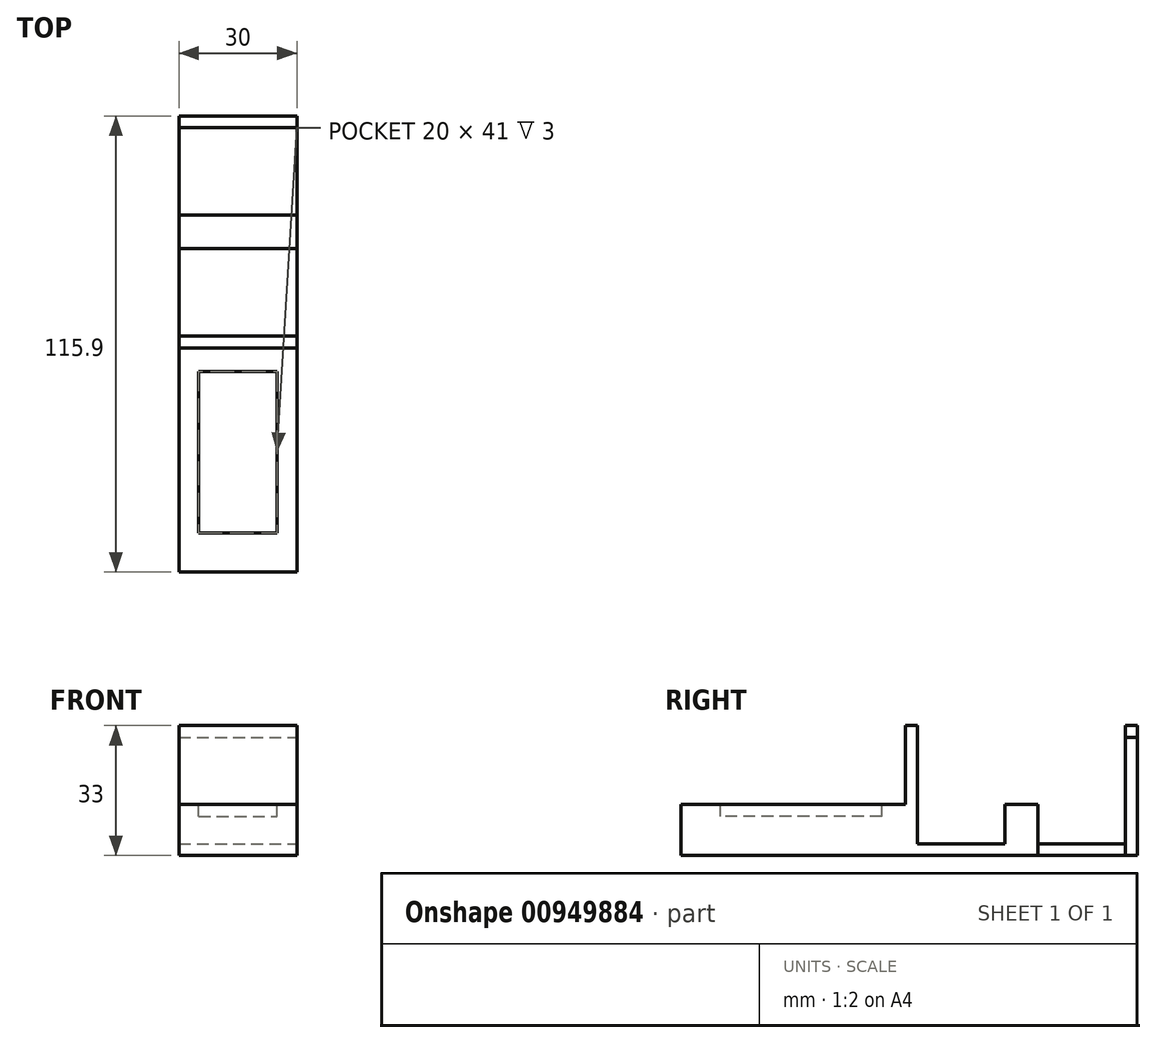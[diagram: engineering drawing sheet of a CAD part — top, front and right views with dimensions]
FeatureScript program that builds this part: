
annotation { "Feature Type Name" : "Feature", "Feature Type Description" : "" }
export const myFeature = defineFeature(function(context is Context, id is Id, definition is map)
    precondition{}
    {
        {
            var Q0;
            Q0=qCreatedBy(makeId("Top.planeOp"),FACE);
            var sketch = newSketch(context, id + "F0", { "sketchPlane" : qUnion([Q0])});
            skLineSegment(sketch, "E0.bottom", {"start": v(82.85, 0) * mm, "end": v(52.85, 0) * mm});
            skLineSegment(sketch, "E0.top", {"start": v(82.85, 115.9) * mm, "end": v(52.85, 115.9) * mm});
            skPoint(sketch, "E0.middle", {"position": v(67.85, 57.95) * mm});
            skLineSegment(sketch, "E1.bottom", {"start": v(52.85, 57) * mm, "end": v(82.85, 57) * mm});
            skLineSegment(sketch, "E1.top", {"start": v(52.85, 60) * mm, "end": v(82.85, 60) * mm});
            skLineSegment(sketch, "E1.left", {"start": v(52.85, 57) * mm, "end": v(52.85, 60) * mm});
            skLineSegment(sketch, "E1.right", {"start": v(82.85, 57) * mm, "end": v(82.85, 60) * mm});
            skLineSegment(sketch, "E2.bottom", {"start": v(52.85, 82.2) * mm, "end": v(82.85, 82.2) * mm});
            skLineSegment(sketch, "E2.top", {"start": v(52.85, 90.7) * mm, "end": v(82.85, 90.7) * mm});
            skLineSegment(sketch, "E2.left", {"start": v(52.85, 82.2) * mm, "end": v(52.85, 90.7) * mm});
            skLineSegment(sketch, "E2.right", {"start": v(82.85, 82.2) * mm, "end": v(82.85, 90.7) * mm});
            skLineSegment(sketch, "E3.bottom", {"start": v(52.85, 112.9) * mm, "end": v(82.85, 112.9) * mm});
            skLineSegment(sketch, "E3.top", {"start": v(52.85, 115.9) * mm, "end": v(82.85, 115.9) * mm});
            skLineSegment(sketch, "E3.left", {"start": v(52.85, 112.9) * mm, "end": v(52.85, 115.9) * mm});
            skLineSegment(sketch, "E3.right", {"start": v(82.85, 112.9) * mm, "end": v(82.85, 115.9) * mm});
            skLineSegment(sketch, "E4", {"start": v(52.85, 0) * mm, "end": v(52.85, 57) * mm});
            skLineSegment(sketch, "E5", {"start": v(52.85, 60) * mm, "end": v(52.85, 82.2) * mm});
            skLineSegment(sketch, "E6", {"start": v(52.85, 90.7) * mm, "end": v(52.85, 112.9) * mm});
            skLineSegment(sketch, "E7", {"start": v(82.85, 112.9) * mm, "end": v(82.85, 90.7) * mm});
            skLineSegment(sketch, "E8", {"start": v(82.85, 82.2) * mm, "end": v(82.85, 60) * mm});
            skLineSegment(sketch, "E9", {"start": v(82.85, 57) * mm, "end": v(82.85, 0) * mm});
            skSolve(sketch);
        }
        {
            var Q0;
            Q0 = qSketchRegion(id + "F0", true);
            extrude(context, id + "F1", {"entities" : qUnion([Q0]), "depth" : 3 * mm, "offsetDistance" : 25 * mm});
        }
        {
            var Q0;
            Q0=makeQuery(id+"F0.imprint","IMPRINT",FACE,{"disambiguationData":[TD([[makeQuery(id+"F0.imprint","IMPRINT",EDGE,{"derivedFrom":sQuery(id+"F0.wireOp",EDGE,"E1.bottom")}),1.0]])]});
            var Q1;
            Q1=makeQuery(id+"F0.imprint","IMPRINT",FACE,{"disambiguationData":[TD([[makeQuery(id+"F0.imprint","IMPRINT",EDGE,{"derivedFrom":sQuery(id+"F0.wireOp",EDGE,"E3.bottom")}),1.0]])]});
            extrude(context, id + "F2", {"entities" : qUnion([Q0, Q1]), "operationType" : NewBodyOperationType.ADD, "depth" : 30 * mm, "offsetDistance" : 25 * mm});
        }
        {
            var Q0;
            Q0=makeQuery(id+"F0.imprint","IMPRINT",FACE,{"disambiguationData":[TD([[makeQuery(id+"F0.imprint","IMPRINT",EDGE,{"derivedFrom":sQuery(id+"F0.wireOp",EDGE,"E2.bottom")}),1.0]])]});
            extrude(context, id + "F3", {"entities" : qUnion([Q0]), "operationType" : NewBodyOperationType.ADD, "depth" : 13 * mm, "offsetDistance" : 25 * mm});
        }
        {
            var Q0;
            {var subQ0=sQuery(id+"F0.wireOp",EDGE,"E9");var subQ1=sQuery(id+"F0.wireOp",EDGE,"E8");var subQ2=sQuery(id+"F0.wireOp",EDGE,"E7");var subQ3=sQuery(id+"F0.wireOp",EDGE,"E3.right");var subQ4=sQuery(id+"F0.wireOp",EDGE,"E2.right");var subQ5=sQuery(id+"F0.wireOp",EDGE,"E1.right");var subQ6=sQuery(id+"F0.wireOp",EDGE,"E6");var subQ7=sQuery(id+"F0.wireOp",EDGE,"E5");var subQ8=sQuery(id+"F0.wireOp",EDGE,"E4");var subQ9=sQuery(id+"F0.wireOp",EDGE,"E3.left");var subQ10=sQuery(id+"F0.wireOp",EDGE,"E2.left");var subQ11=sQuery(id+"F0.wireOp",EDGE,"E1.left");var subQ12=sQuery(id+"F0.wireOp",EDGE,"E0.bottom");Q0=makeQuery(id+"F2.boolean.opBoolean","SPLIT",FACE,{"disambiguationData":[TD([makeQuery(id+"F1.opExtrude","SWEPT_FACE",FACE,{"disambiguationData":[OSD([subQ12])]})])],"derivedFrom":makeQuery(id+"F1.opExtrude","CAP_FACE",FACE,{"disambiguationData":[OSD([subQ12,subQ11,subQ5,subQ10,subQ4,sQuery(id+"F0.wireOp",EDGE,"E3.top"),subQ9,subQ3,subQ8,subQ7,subQ6,subQ2,subQ1,subQ0])],"isStart":false})});}
            extrude(context, id + "F4", {"entities" : qUnion([Q0]), "operationType" : NewBodyOperationType.ADD, "depth" : 10 * mm, "offsetDistance" : 25 * mm});
        }
        {
            var Q0;
            Q0=makeQuery(id+"F4.opExtrude","CAP_FACE",FACE,{"disambiguationData":[OSD([sQuery(id+"F0.wireOp",EDGE,"E0.bottom"),sQuery(id+"F0.wireOp",EDGE,"E1.left"),sQuery(id+"F0.wireOp",EDGE,"E1.right"),sQuery(id+"F0.wireOp",EDGE,"E2.left"),sQuery(id+"F0.wireOp",EDGE,"E2.right"),sQuery(id+"F0.wireOp",EDGE,"E3.top"),sQuery(id+"F0.wireOp",EDGE,"E3.left"),sQuery(id+"F0.wireOp",EDGE,"E3.right"),sQuery(id+"F0.wireOp",EDGE,"E4"),sQuery(id+"F0.wireOp",EDGE,"E5"),sQuery(id+"F0.wireOp",EDGE,"E6"),sQuery(id+"F0.wireOp",EDGE,"E7"),sQuery(id+"F0.wireOp",EDGE,"E8"),sQuery(id+"F0.wireOp",EDGE,"E9")])],"isStart":false});
            var sketch = newSketch(context, id + "F5", { "sketchPlane" : qUnion([Q0])});
            skLineSegment(sketch, "E10.bottom", {"start": v(77.85, 10) * mm, "end": v(57.85, 10) * mm});
            skLineSegment(sketch, "E10.top", {"start": v(77.85, 51) * mm, "end": v(57.85, 51) * mm});
            skLineSegment(sketch, "E10.left", {"start": v(77.85, 10) * mm, "end": v(77.85, 51) * mm});
            skLineSegment(sketch, "E10.right", {"start": v(57.85, 10) * mm, "end": v(57.85, 51) * mm});
            skPoint(sketch, "E10.middle", {"position": v(67.85, 30.5) * mm});
            skSolve(sketch);
        }
        {
            var Q0;
            Q0=makeQuery(id+"F5.imprint","IMPRINT",FACE,{"disambiguationData":[TD([[makeQuery(id+"F5.imprint","IMPRINT",EDGE,{"derivedFrom":sQuery(id+"F5.wireOp",EDGE,"E10.bottom")}),-1.0]])]});
            extrude(context, id + "F6", {"entities" : qUnion([Q0]), "operationType" : NewBodyOperationType.REMOVE, "endBound" : BoundingType.UP_TO_NEXT, "oppositeDirection" : true, "depth" : 25 * mm, "offsetDistance" : 25 * mm});
        }
        {
            var Q0;
            Q0=makeQuery(id+"F0.imprint","IMPRINT",FACE,{"disambiguationData":[TD([[makeQuery(id+"F0.imprint","IMPRINT",EDGE,{"derivedFrom":sQuery(id+"F0.wireOp",EDGE,"E1.bottom")}),1.0]])]});
            var Q1;
            Q1=makeQuery(id+"F0.imprint","IMPRINT",FACE,{"disambiguationData":[TD([[makeQuery(id+"F0.imprint","IMPRINT",EDGE,{"derivedFrom":sQuery(id+"F0.wireOp",EDGE,"E3.bottom")}),1.0]])]});
            extrude(context, id + "F7", {"entities" : qUnion([Q0, Q1]), "depth" : 33 * mm, "offsetDistance" : 25 * mm});
        }
        {
            var Q0;
            Q0=makeQuery(id+"F0.imprint","IMPRINT",FACE,{"disambiguationData":[TD([[makeQuery(id+"F0.imprint","IMPRINT",EDGE,{"derivedFrom":sQuery(id+"F0.wireOp",EDGE,"E2.bottom")}),1.0]])]});
            extrude(context, id + "F8", {"entities" : qUnion([Q0]), "depth" : 13 * mm, "offsetDistance" : 25 * mm});
        }
        {
            var Q0;
            Q0=makeQuery(id+"F0.imprint","IMPRINT",FACE,{"disambiguationData":[TD([[makeQuery(id+"F0.imprint","IMPRINT",EDGE,{"derivedFrom":sQuery(id+"F0.wireOp",EDGE,"E0.bottom")}),-1.0]])]});
            extrude(context, id + "F9", {"entities" : qUnion([Q0]), "depth" : 10 * mm, "offsetDistance" : 25 * mm});
        }
        {
            var Q0;
            Q0=makeQuery(id+"F0.imprint","IMPRINT",FACE,{"disambiguationData":[TD([[makeQuery(id+"F0.imprint","IMPRINT",EDGE,{"derivedFrom":sQuery(id+"F0.wireOp",EDGE,"E1.bottom")}),1.0]])]});
            extrude(context, id + "F10", {"entities" : qUnion([Q0]), "operationType" : NewBodyOperationType.ADD, "depth" : 30 * mm, "offsetDistance" : 25 * mm});
        }
        {
            var Q0;
            Q0=makeQuery(id+"F0.imprint","IMPRINT",FACE,{"disambiguationData":[TD([[makeQuery(id+"F0.imprint","IMPRINT",EDGE,{"derivedFrom":sQuery(id+"F0.wireOp",EDGE,"E1.top")}),1.0]])]});
            extrude(context, id + "F11", {"entities" : qUnion([Q0]), "operationType" : NewBodyOperationType.ADD, "depth" : 3 * mm, "offsetDistance" : 25 * mm});
        }
        {
            var Q0;
            Q0=makeQuery(id+"F0.imprint","IMPRINT",FACE,{"disambiguationData":[TD([[makeQuery(id+"F0.imprint","IMPRINT",EDGE,{"derivedFrom":sQuery(id+"F0.wireOp",EDGE,"E2.bottom")}),1.0]])]});
            extrude(context, id + "F12", {"entities" : qUnion([Q0]), "operationType" : NewBodyOperationType.ADD, "depth" : 13 * mm, "offsetDistance" : 25 * mm});
        }
        {
            var Q0;
            Q0=makeQuery(id+"F0.imprint","IMPRINT",FACE,{"disambiguationData":[TD([[makeQuery(id+"F0.imprint","IMPRINT",EDGE,{"derivedFrom":sQuery(id+"F0.wireOp",EDGE,"E3.bottom")}),1.0]])]});
            extrude(context, id + "F13", {"entities" : qUnion([Q0]), "depth" : 30 * mm, "offsetDistance" : 25 * mm});
        }
        {
            var Q0;
            Q0=makeQuery(id+"F0.imprint","IMPRINT",FACE,{"disambiguationData":[TD([[makeQuery(id+"F0.imprint","IMPRINT",EDGE,{"derivedFrom":sQuery(id+"F0.wireOp",EDGE,"E2.top")}),1.0]])]});
            extrude(context, id + "F14", {"entities" : qUnion([Q0]), "depth" : 3 * mm, "offsetDistance" : 25 * mm});
        }
    });
